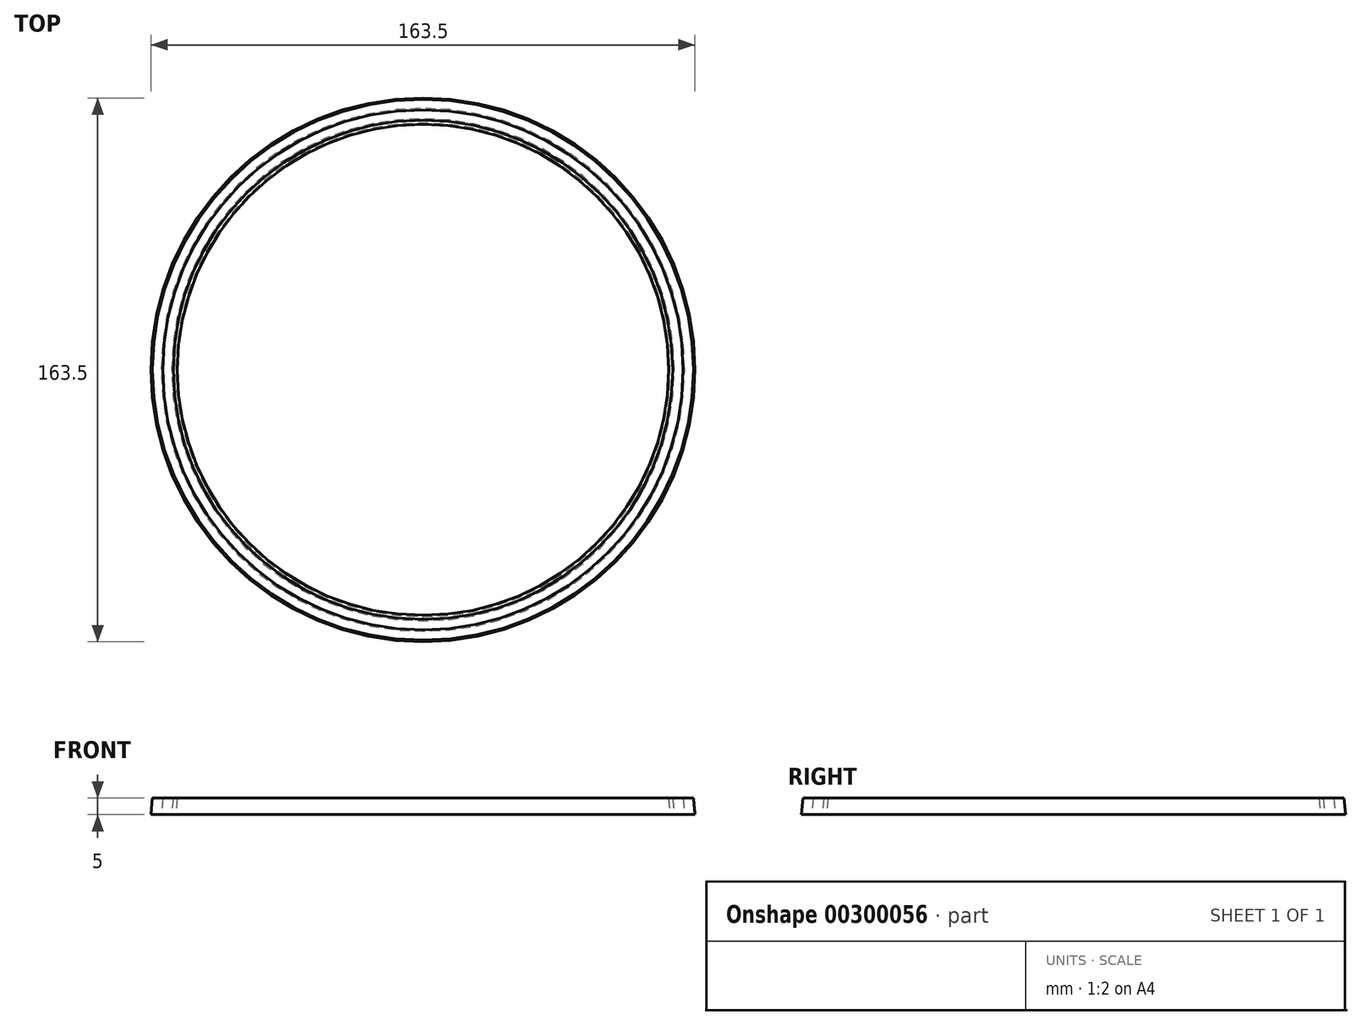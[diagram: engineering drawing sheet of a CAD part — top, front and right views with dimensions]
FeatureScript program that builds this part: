
annotation { "Feature Type Name" : "Feature", "Feature Type Description" : "" }
export const myFeature = defineFeature(function(context is Context, id is Id, definition is map)
    precondition{}
    {
        {
            assignVariable(context, id + "F0", {"name" : "bucket_t", "anyValue" : 0.75});
        }
        {
            assignVariable(context, id + "F1", {"name" : "bucket_top_d", "anyValue" : 165 - (getVariable(context, 'bucket_t') * 2)});
        }
        {
            assignVariable(context, id + "F2", {"name" : "bucket_bot_d", "anyValue" : 140 - (getVariable(context, 'bucket_t') * 2)});
        }
        {
            assignVariable(context, id + "F3", {"name" : "bucket_h", "anyValue" : 140});
        }
        {
            assignVariable(context, id + "F4", {"name" : "bucket_angle", "anyValue" : atan(((getVariable(context, 'bucket_top_d') - getVariable(context, 'bucket_bot_d')) / 2) / getVariable(context, 'bucket_h'))});
        }
        {
            assignVariable(context, id + "F5", {"name" : "spacer_h", "anyValue" : 5});
        }
        {
            var Q0;
            Q0=qCreatedBy(makeId("Top.planeOp"),FACE);
            var sketch = newSketch(context, id + "F6", { "sketchPlane" : qUnion([Q0])});
            skCircle(sketch, "E0", {"center": v(0, 0) * mm, "radius": 81.75 * mm});
            skSolve(sketch);
        }
        {
            var Q0;
            Q0=qSketchRegion(id+"F6",true);
            extrude(context, id + "F7", {"entities" : qUnion([Q0]), "depth" : (getVariable(context, 'spacer_h')) * mm, "hasDraft" : true, "draftAngle" : getVariable(context, 'bucket_angle'), "draftPullDirection" : true});
        }
        {
            var Q0;
            Q0=qCreatedBy(makeId("Top.planeOp"),FACE);
            var sketch = newSketch(context, id + "F8", { "sketchPlane" : qUnion([Q0])});
            skCircle(sketch, "E1", {"center": v(0, 0) * mm, "radius": 78.62 * mm});
            skSolve(sketch);
        }
        {
            var Q0;
            Q0=qSketchRegion(id+"F8",true);
            extrude(context, id + "F9", {"entities" : qUnion([Q0]), "depth" : (getVariable(context, 'spacer_h')) * mm, "hasDraft" : true, "draftAngle" : getVariable(context, 'bucket_angle'), "draftPullDirection" : true});
        }
        {
            var Q0;
            Q0=qCreatedBy(makeId("Top.planeOp"),FACE);
            var sketch = newSketch(context, id + "F10", { "sketchPlane" : qUnion([Q0])});
            skCircle(sketch, "E2", {"center": v(0, 0) * mm, "radius": 75.5 * mm});
            skSolve(sketch);
        }
        {
            var Q0;
            Q0=qSketchRegion(id+"F10",true);
            extrude(context, id + "F11", {"entities" : qUnion([Q0]), "depth" : (getVariable(context, 'spacer_h')) * mm, "hasDraft" : true, "draftAngle" : getVariable(context, 'bucket_angle'), "draftPullDirection" : true});
        }
        {
            var Q0;
            Q0=qCreatedBy(makeId("Top.planeOp"),FACE);
            var sketch = newSketch(context, id + "F12", { "sketchPlane" : qUnion([Q0])});
            skCircle(sketch, "E3", {"center": v(0, 0) * mm, "radius": 74.25 * mm});
            skSolve(sketch);
        }
        {
            var Q0;
            Q0=makeQuery(id+"F12.imprint","IMPRINT",FACE,{"disambiguationData":[TD([[makeQuery(id+"F12.imprint","IMPRINT",EDGE,{"derivedFrom":sQuery(id+"F12.wireOp",EDGE,"E3")}),1.0]])]});
            extrude(context, id + "F13", {"entities" : qUnion([Q0]), "depth" : (getVariable(context, 'spacer_h')) * mm, "hasDraft" : true, "draftAngle" : getVariable(context, 'bucket_angle'), "draftPullDirection" : true});
        }
    });
